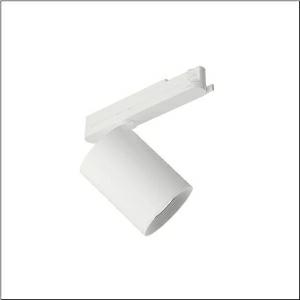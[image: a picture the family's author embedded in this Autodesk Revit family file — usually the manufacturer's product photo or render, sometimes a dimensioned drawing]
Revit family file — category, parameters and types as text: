
# Revit family: spot_21_51se13mba5b
name_source: partatom
category: Lighting Fixtures
units: mm (PartAtom-declared; Revit-internal decimal feet)

## family parameters
Cut with Voids When Loaded = No
Host = Face
Light Source = No
Part Type = Normal
Room Calculation Point = No
Round Connector Dimension = Use Diameter
Shared = No

## types (1)
- --- (1 x LED, 5300 lm, 41.8 W, 2700K)
    Apparent Load = 42 VA
    CIE Flux Codes = 95 98 99 100 100
    Color Rendering = 90
    Color Temperature = 2700K
    Default Elevation = 1800 mm
    Description = Spot 21, directional spotlight, light control with lens, of PMMA, LED rated luminous flux: 5.090lm, light colour: 927, control gear: ECG Multilumen, with 3-phase adapter, mains connection: 220..240V, AC, 50/60Hz, of aluminium, traffic white (RAL 9016), length: 213mm, diameter: 105mm, protection rating (complete): IP20, insulation class (complete): insulation class I (protective earthing), certification: CE, impact resistance: IK02, permissible ambient temperature for indoor applications: -20..+40°C, packaging unit: 1 piece
    Height = 175 mm
    Lamp = 1 x LED
    Lamp Light Flux = 5300 lm
    Lamp Power = 41.8 W
    Lamp count = 1
    Length = 105 mm
    Luminous efficacy = 127 lm/W
    Manufacturer = Siteco
    ModVariant = No
    Model = 51SE13MBA5B
    Mounting Place = Ceiling
    Mounting Type = Pendant
    Number of Poles = 1
    OnlyDefault = Yes
    Power Factor = 1
    Product Name = Spot 21
    Product group = directional spotlight
    ProductGroupID = 905
    Protection Class = Protection class I
    Protection Degree = IP 20
    RLX_Detail_Level = 1
    RLX_Emergency_Light_Flux = 0 lm
    RLX_Emergency_Type = 0
    RLX_Emergency_Type_DB = No
    RlxData = <blob elided: 17605 chars, md5=938f5de4>
    Socket = socket
    Standby Power = 0 W
    System Light Flux = 5300 lm
    System Power = 42 W
    Type Comments = factory setting: luminous flux: 100 % | (ON | ON | ON | ON) | 1050 mA
    Type Image = l_1003976.jpg
    URL = http://relux.com
    VarID = @adj_165697
    Voltage = 0 V
    Weight = 0.00 kg
    Width = 0 mm  [stored 0 ft]

note: [stored X ft] marks values corroborated as IEEE doubles in the binary element streams (Revit-internal decimal feet)

## geometry (parser evidence)
native form markers: Blend x4, Sweep x9
no freeform markers — native parametric forms only
